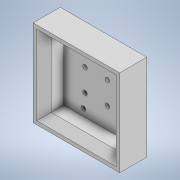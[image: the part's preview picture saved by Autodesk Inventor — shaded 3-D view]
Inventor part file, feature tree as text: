
AUTODESK INVENTOR PART (.ipt)
format: ipt  version: 2021 (Build 250183000, 183)  size: 146,944 bytes
history: native  units: in
note: dims shown in document units (in); Inventor stores cm internally (conversion verified against a paired STEP export)
features: extrude x3, sketch x3, chamfer x1
ambient origin geometry x8: Origin, YZ Plane, XZ Plane, XY Plane, X Axis, Y Axis, Z Axis, Center Point
bodies: Solid1 (feature_tree)
feature tree (7):
  extrude  "Extrusion1"  Depth=1.8898in
  extrude  "Extrusion2"  Depth=1.4173in
  chamfer  "Chamfer1"  Distance=0.4331in
  sketch  "Sketch3"  dims[d7=1.4173in d8=0.4331in d9=0.0in d10=0.1575in d11=0.0787in d12=45.0deg d21=0.0315in d22=0.1417in d23=0.063in d25=0.1417in d26=0.063in d27=0.1417in d28=0.063in d30=0.063in d46=0.1969in d47=0.0in d62=0.0984in d63=0.0984in d64=0.0984in d65=0.0984in d66=0.0984in d67=0.0984in d44=0.0197in d45=0.0344in]
  extrude  "Extrusion4"  Depth=0.1575in TaperAngle=45.0deg
  sketch  "Sketch1"  dims[d0=1.8898in d1=1.8898in]
  sketch  "Sketch2"  dims[d2=0.5906in d3=0.0in d6=1.4173in]
